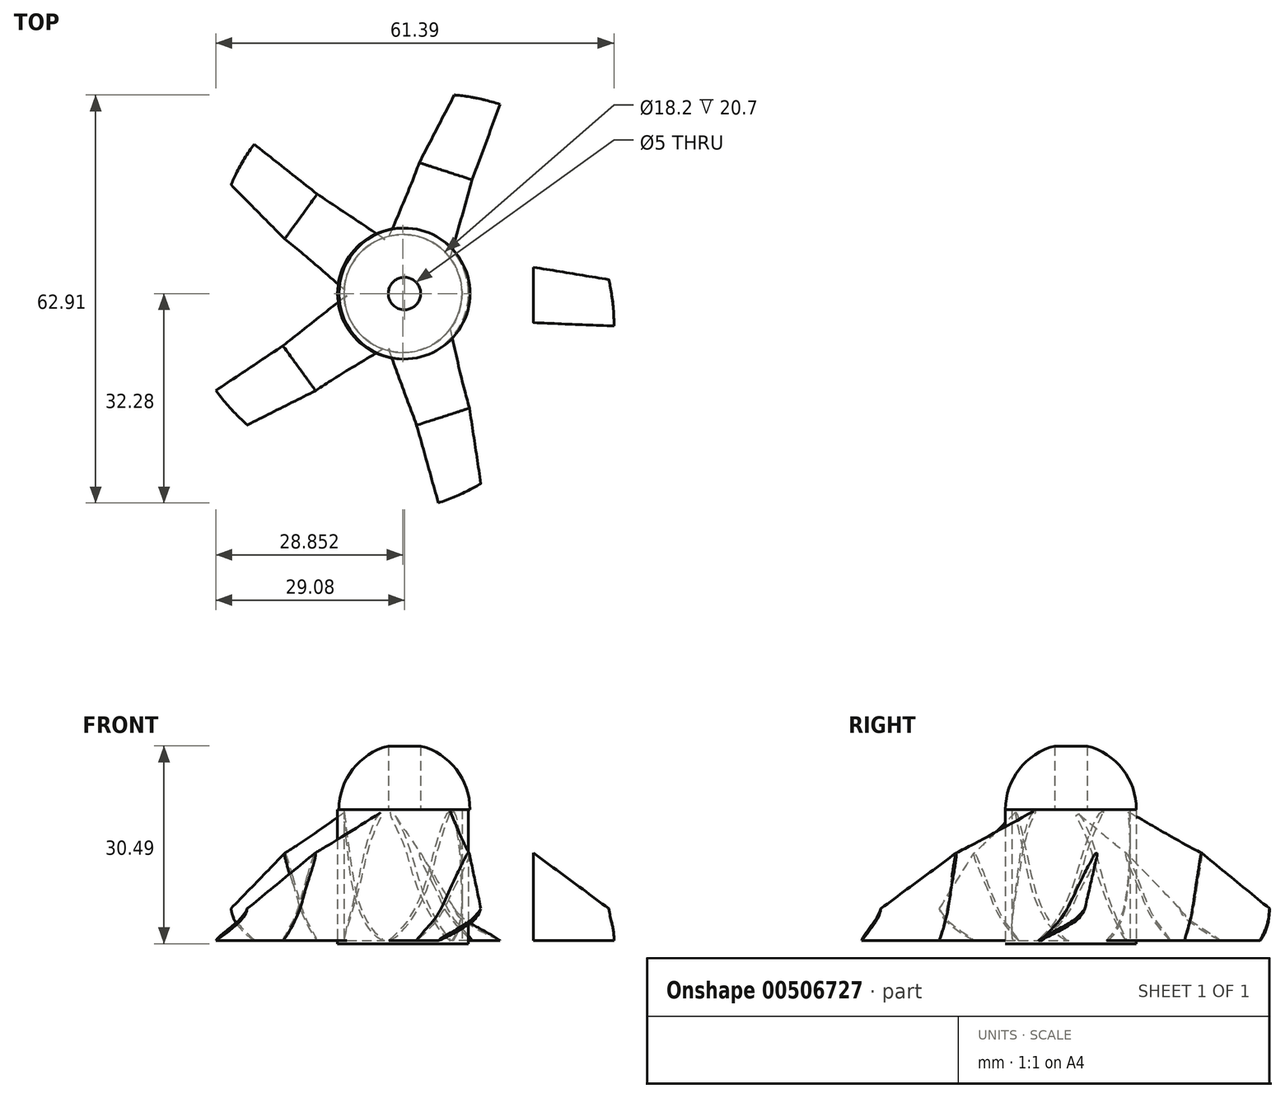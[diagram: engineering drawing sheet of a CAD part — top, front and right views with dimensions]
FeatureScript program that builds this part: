
annotation { "Feature Type Name" : "Feature", "Feature Type Description" : "" }
export const myFeature = defineFeature(function(context is Context, id is Id, definition is map)
    precondition{}
    {
        {
            var Q0;
            Q0=qCreatedBy(makeId("Right.planeOp"),FACE);
            var sketch = newSketch(context, id + "F0", { "sketchPlane" : qUnion([Q0])});
            skLineSegment(sketch, "E0.bottom", {"start": v(0, 0) * mm, "end": v(10, 0) * mm, "construction": true});
            skLineSegment(sketch, "E0.top", {"start": v(0, 20) * mm, "end": v(10, 20) * mm, "construction": true});
            skLineSegment(sketch, "E0.left", {"start": v(0, 0) * mm, "end": v(0, 20) * mm, "construction": true});
            skLineSegment(sketch, "E0.right", {"start": v(10, 0) * mm, "end": v(10, 20) * mm, "construction": true});
            skFitSpline(sketch, "E1", {"points": [v(0, 0) * mm, v(1.35, 1.46) * mm, v(3.44, 4.56) * mm, v(5.27, 8.57) * mm, v(6.9, 14.19) * mm, v(9.62, 20) * mm, v(10, 19.9) * mm, v(9.67, 19.13) * mm, v(8.8, 17.32) * mm, v(7.67, 14.46) * mm, v(6.57, 10.48) * mm, v(3.61, 3.91) * mm, v(0.61, 0.3) * mm, v(0, 0) * mm]});
            skSolve(sketch);
        }
        {
            var Q0;
            Q0=qCreatedBy(makeId("Right.planeOp"),FACE);
            cPlane(context, id + "F1", {"entities" : qUnion([Q0]), "cplaneType" : CPlaneType.OFFSET, "offset" : 12.5 * mm, "width" : 150 * mm, "height" : 150 * mm});
        }
        {
            var Q0;
            Q0=qCreatedBy(id+"F1.planeOp",FACE);
            var sketch = newSketch(context, id + "F2", { "sketchPlane" : qUnion([Q0])});
            skLineSegment(sketch, "E2.0", {"start": v(9, 0) * mm, "end": v(9, 20) * mm, "construction": true});
            skFitSpline(sketch, "E3", {"points": [v(0.5, 0) * mm, v(2.27, 2.03) * mm, v(4.13, 4.36) * mm, v(6.73, 9.59) * mm, v(8.45, 12.9) * mm, v(8.8, 13.41) * mm, v(9, 13.47) * mm, v(9, 12.94) * mm, v(6.9, 8.74) * mm, v(5.74, 6.4) * mm, v(3.55, 2.91) * mm, v(0.5, 0) * mm]});
            skLineSegment(sketch, "E4.0", {"start": v(0.5, 0) * mm, "end": v(0.5, 20) * mm, "construction": true});
            skSolve(sketch);
        }
        {
            var Q0;
            Q0=qCreatedBy(id+"F1.planeOp",FACE);
            cPlane(context, id + "F3", {"entities" : qUnion([Q0]), "cplaneType" : CPlaneType.OFFSET, "offset" : 12.5 * mm, "width" : 150 * mm, "height" : 150 * mm});
        }
        {
            var Q0;
            Q0=qCreatedBy(id+"F3.planeOp",FACE);
            var sketch = newSketch(context, id + "F4", { "sketchPlane" : qUnion([Q0])});
            skLineSegment(sketch, "E5.0", {"start": v(7, 0) * mm, "end": v(7, 20) * mm});
            skFitSpline(sketch, "E6", {"points": [v(0, 0) * mm, v(1.24, 0.75) * mm, v(3.76, 2.1) * mm, v(5.78, 3.31) * mm, v(6.7, 4.12) * mm, v(7, 4.27) * mm, v(6.46, 3.5) * mm, v(5.25, 2.6) * mm, v(2.92, 1.29) * mm, v(1.38, 0.56) * mm, v(0, 0) * mm]});
            skSolve(sketch);
        }
        {
            var Q0;
            Q0 = qSketchRegion(id + "F0", true);
            var Q1;
            Q1 = qSketchRegion(id + "F2", true);
            loft(context, id + "F5", {"sheetProfilesArray" : [{ "sheetProfileEntities" : qUnion([Q0]) }, { "sheetProfileEntities" : qUnion([Q1]) }]});
        }
        {
            var Q0;
            Q0 = qSketchRegion(id + "F2", true);
            var Q1;
            Q1 = qSketchRegion(id + "F4", true);
            var Q2;
            Q2=sQuery(id+"F2.wireOp",VERTEX,"E3.0.internal");
            var Q3;
            Q3=sQuery(id+"F4.wireOp",VERTEX,"E6.0.internal");
            loft(context, id + "F6", {"operationType" : NewBodyOperationType.ADD, "sheetProfilesArray" : [{ "sheetProfileEntities" : qUnion([Q0]) }, { "sheetProfileEntities" : qUnion([Q1]) }], "matchConnections" : true, "connections" : [{ "connectionEntities" : qUnion([Q2, Q3]), "connectionEdgeQueries" : qUnion([]), "connectionEdgeParameters" : [] }]});
        }
        {
            var Q0;
            Q0=qCreatedBy(makeId("Top.planeOp"),FACE);
            cPlane(context, id + "F7", {"entities" : qUnion([Q0]), "cplaneType" : CPlaneType.OFFSET, "offset" : 5 * mm, "oppositeDirection" : true, "width" : 150 * mm, "height" : 150 * mm});
        }
        {
            var Q0;
            Q0=qCreatedBy(id+"F7.planeOp",FACE);
            var sketch = newSketch(context, id + "F8", { "sketchPlane" : qUnion([Q0])});
            skArc(sketch, "E7", {"start": v(24.91, 0) * mm, "mid": v(24.7, 3.6) * mm, "end": v(24.1, 7.17) * mm});
            skLineSegment(sketch, "E8", {"start": v(24.1, 7.17) * mm, "end": v(27.5, 7.17) * mm});
            skLineSegment(sketch, "E9", {"start": v(27.5, 7.17) * mm, "end": v(27.5, 0) * mm});
            skLineSegment(sketch, "E10", {"start": v(27.5, 0) * mm, "end": v(24.91, 0) * mm});
            skLineSegment(sketch, "E11", {"start": v(24.91, 0) * mm, "end": v(24.91, 0) * mm});
            skSolve(sketch);
        }
        {
            var Q0;
            Q0=makeQuery(id+"F8.imprint","IMPRINT",FACE,{"disambiguationData":[TD([[makeQuery(id+"F8.imprint","IMPRINT",EDGE,{"derivedFrom":sQuery(id+"F8.wireOp",EDGE,"E7")}),-1.0]])]});
            extrude(context, id + "F9", {"entities" : qUnion([Q0]), "operationType" : NewBodyOperationType.REMOVE, "depth" : 25 * mm, "offsetDistance" : 25 * mm});
        }
        {
            var Q0;
            Q0=qCreatedBy(makeId("Top.planeOp"),FACE);
            var sketch = newSketch(context, id + "F10", { "sketchPlane" : qUnion([Q0])});
            skLineSegment(sketch, "E12", {"start": v(-7.63, 0) * mm, "end": v(-7.63, 5) * mm, "construction": true});
            skCircle(sketch, "E13", {"center": v(-7.63, 5) * mm, "radius": 10.1 * mm});
            skSolve(sketch);
        }
        {
            var Q0;
            Q0=qCreatedBy(makeId("Front.planeOp"),FACE);
            cPlane(context, id + "F11", {"entities" : qUnion([Q0]), "cplaneType" : CPlaneType.OFFSET, "offset" : 5 * mm, "oppositeDirection" : true, "width" : 150 * mm, "height" : 150 * mm});
        }
        {
            var Q0;
            Q0=qCreatedBy(makeId("Front.planeOp"),FACE);
            var sketch = newSketch(context, id + "F12", { "sketchPlane" : qUnion([Q0])});
            skLineSegment(sketch, "E14", {"start": v(0, 0) * mm, "end": v(-7.4, 0) * mm, "construction": true});
            skLineSegment(sketch, "E15", {"start": v(-7.4, 0) * mm, "end": v(-7.4, 35.57) * mm, "construction": true});
            skSolve(sketch);
        }
        {
            var Q0;
            Q0=qCreatedBy(id+"F11.planeOp",FACE);
            var sketch = newSketch(context, id + "F13", { "sketchPlane" : qUnion([Q0])});
            skLineSegment(sketch, "E16.0", {"start": v(-7.4, 0) * mm, "end": v(-7.4, 35.57) * mm, "construction": true});
            skSolve(sketch);
        }
        {
            var Q0;
            Q0=makeQuery(id+"F5.opLoft","SWEPT_BODY",BODY,{"disambiguationData":[OSD([makeQuery(id+"F0.imprint","IMPRINT",FACE,{"disambiguationData":[TD([[makeQuery(id+"F0.imprint","IMPRINT",EDGE,{"derivedFrom":sQuery(id+"F0.wireOp",EDGE,"E1")}),-1.0]])]}),makeQuery(id+"F2.imprint","IMPRINT",FACE,{"disambiguationData":[TD([[makeQuery(id+"F2.imprint","IMPRINT",EDGE,{"derivedFrom":sQuery(id+"F2.wireOp",EDGE,"E3")}),-1.0]])]})])]});
            var Q1;
            Q1=sQuery(id+"F13.wireOp",EDGE,"E16.0");
            circularPattern(context, id + "F14", {"entities" : qUnion([Q0]), "axis" : qUnion([Q1]), "angle" : 360 * degree, "instanceCount" : 5, "equalSpace" : true});
        }
        {
            var Q0;
            Q0=qCreatedBy(makeId("Top.planeOp"),FACE);
            var sketch = newSketch(context, id + "F15", { "sketchPlane" : qUnion([Q0])});
            skCircle(sketch, "E17.0", {"center": v(-7.63, 5) * mm, "radius": 10.1 * mm});
            skCircle(sketch, "E18.0", {"center": v(-7.63, 5) * mm, "radius": 9.1 * mm});
            skCircle(sketch, "E19", {"center": v(-7.63, 5) * mm, "radius": 2.5 * mm});
            skSolve(sketch);
        }
        {
            var Q0;
            Q0=makeQuery(id+"F15.imprint","IMPRINT",FACE,{"disambiguationData":[TD([[makeQuery(id+"F15.imprint","IMPRINT",EDGE,{"derivedFrom":sQuery(id+"F15.wireOp",EDGE,"E18.0")}),1.0]])]});
            extrude(context, id + "F16", {"entities" : qUnion([Q0]), "operationType" : NewBodyOperationType.REMOVE, "depth" : 25 * mm, "offsetDistance" : 25 * mm});
        }
        {
            var Q0;
            Q0=makeQuery(id+"F15.imprint","IMPRINT",FACE,{"disambiguationData":[TD([[makeQuery(id+"F15.imprint","IMPRINT",EDGE,{"derivedFrom":sQuery(id+"F15.wireOp",EDGE,"E17.0")}),1.0]])]});
            extrude(context, id + "F17", {"entities" : qUnion([Q0]), "depth" : 20.2 * mm, "offsetDistance" : 25 * mm, "hasSecondDirection" : true, "secondDirectionOppositeDirection" : true, "secondDirectionDepth" : .5 * mm});
        }
        {
            var Q0;
            Q0=qCreatedBy(makeId("Right.planeOp"),FACE);
            cPlane(context, id + "F18", {"entities" : qUnion([Q0]), "cplaneType" : CPlaneType.OFFSET, "offset" : 7.4 * mm, "oppositeDirection" : true, "width" : 150 * mm, "height" : 150 * mm});
        }
        {
            var Q0;
            Q0=qCreatedBy(id+"F18.planeOp",FACE);
            var sketch = newSketch(context, id + "F19", { "sketchPlane" : qUnion([Q0])});
            skLineSegment(sketch, "E20.0", {"start": v(-5.1, 20.2) * mm, "end": v(2.5, 20.2) * mm});
            skArc(sketch, "E21", {"start": v(2.5, 29.99) * mm, "mid": v(-2.98, 26.4) * mm, "end": v(-5.1, 20.2) * mm});
            skLineSegment(sketch, "E22.0", {"start": v(2.5, 0) * mm, "end": v(2.5, 35.57) * mm, "construction": true});
            skLineSegment(sketch, "E23", {"start": v(2.5, 20.2) * mm, "end": v(2.5, 29.99) * mm});
            skLineSegment(sketch, "E24.trimOffspring", {"start": v(5, 20.2) * mm, "end": v(15.1, 20.2) * mm});
            skSolve(sketch);
        }
        {
            var Q0;
            Q0=makeQuery(id+"F19.imprint","IMPRINT",FACE,{"disambiguationData":[TD([[makeQuery(id+"F19.imprint","IMPRINT",EDGE,{"derivedFrom":sQuery(id+"F19.wireOp",EDGE,"E20.0")}),1.0]])]});
            var Q1;
            Q1=sQuery(id+"F13.wireOp",EDGE,"E16.0");
            revolve(context, id + "F20", {"operationType" : NewBodyOperationType.ADD, "surfaceOperationType" : NewSurfaceOperationType.NEW, "entities" : qUnion([Q0]), "axis" : qUnion([Q1]), "revolveType" : RevolveType.FULL});
        }
    });
